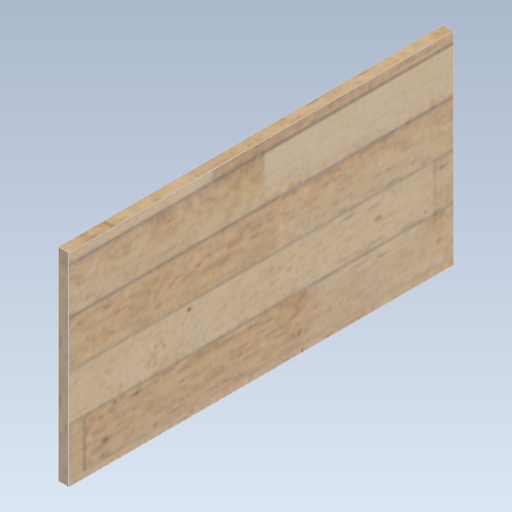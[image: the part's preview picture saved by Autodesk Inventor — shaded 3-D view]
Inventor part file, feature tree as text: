
AUTODESK INVENTOR PART (.ipt)
format: ipt  version: 2021 (Build 250183000, 183)  size: 262,656 bytes
history: native  units: mm
features: extrude x1, sketch x1
ambient origin geometry x8: Origin, YZ Plane, XZ Plane, XY Plane, X Axis, Y Axis, Z Axis, Center Point
bodies: Solid1 (feature_tree)
feature tree (2):
  extrude  "Extrusion1"  [1 undecoded]
  sketch  "Sketch1"  dims[d3=0.0mm]
note: 1 required parameter value undecoded (feature->parameter linkage not recoverable at this tier; creation-order binding heuristic only, values carry confidence <= 0.55)
